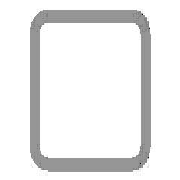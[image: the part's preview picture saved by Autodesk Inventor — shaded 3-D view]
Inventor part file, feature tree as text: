
AUTODESK INVENTOR PART (.ipt)
format: ipt  version: 2025 (Build 290162010, 162A)  size: 133,632 bytes
history: native  units: mm (DEFAULTED — no unit token found)
features: other x4, sketch x1, plane x1
ambient origin geometry x8: Origin, YZ Plane, XZ Plane, XY Plane, X Axis, Y Axis, Z Axis, Center Point
bodies: Solid1 (feature_tree), Body (feature_tree)
feature tree (6):
  parser-record x1  (decoder bookkeeping rows leaked as tree rows — omitted from the tree; the rows remain in map.json)
  other  "Driven Length"
  other  "Start Plane"
  other  "End Plane"
  sketch  "Sketch3"  dims[d3=3200.0mm d4=0.0mm d7=6.0mm d9=80.0mm d11=80.0mm d12=3.0mm d13=-0.0mm d14=3200.0mm d15=40.0mm d16=40.0mm d17=90.0deg d18=3200.0mm]
  plane  "Work Plane3"
